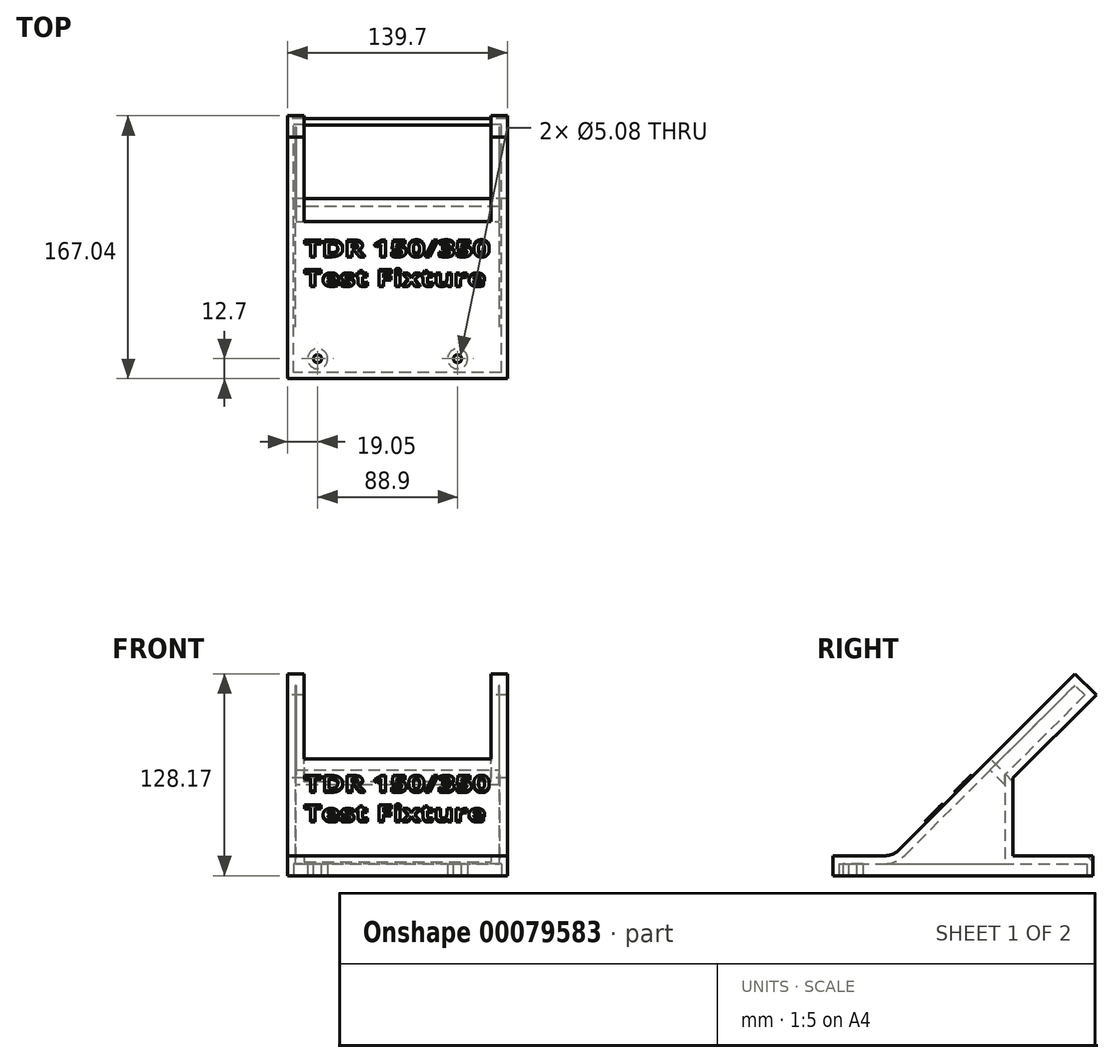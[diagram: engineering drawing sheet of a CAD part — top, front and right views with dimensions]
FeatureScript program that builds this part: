
annotation { "Feature Type Name" : "Feature", "Feature Type Description" : "" }
export const myFeature = defineFeature(function(context is Context, id is Id, definition is map)
    precondition{}
    {
        {
            var Q0;
            Q0=qCreatedBy(makeId("Right.planeOp"),FACE);
            var sketch = newSketch(context, id + "F0", { "sketchPlane" : qUnion([Q0])});
            skLineSegment(sketch, "E0.bottom", {"start": v(0, 0) * mm, "end": v(165.1, 0) * mm});
            skLineSegment(sketch, "E0.top", {"start": v(0, 12.7) * mm, "end": v(32.84, 12.7) * mm});
            skLineSegment(sketch, "E0.left", {"start": v(0, 0) * mm, "end": v(0, 12.7) * mm});
            skLineSegment(sketch, "E0.right", {"start": v(165.1, 0) * mm, "end": v(165.1, 12.7) * mm});
            skLineSegment(sketch, "E1", {"start": v(41.82, 16.42) * mm, "end": v(145.86, 120.46) * mm});
            skLineSegment(sketch, "E2.0", {"start": v(114.33, 61.98) * mm, "end": v(167.04, 114.7) * mm});
            skLineSegment(sketch, "E3.trimOffspring", {"start": v(114.33, 12.7) * mm, "end": v(165.1, 12.7) * mm});
            skPoint(sketch, "E4.visualSharp", {"position": v(38.1, 12.7) * mm});
            skArc(sketch, "E4.filletArc", {"start": v(32.84, 12.7) * mm, "mid": v(37.7, 13.67) * mm, "end": v(41.82, 16.42) * mm});
            skPoint(sketch, "E5.visualSharp", {"position": v(65.04, 12.7) * mm});
            skLineSegment(sketch, "E6", {"start": v(145.86, 120.46) * mm, "end": v(153.57, 128.17) * mm});
            skLineSegment(sketch, "E7", {"start": v(167.04, 114.7) * mm, "end": v(153.57, 128.17) * mm});
            skLineSegment(sketch, "E8", {"start": v(114.33, 61.98) * mm, "end": v(114.33, 12.7) * mm});
            skSolve(sketch);
        }
        {
            var Q0;
            Q0=makeQuery(id+"F0.imprint","IMPRINT",FACE,{"disambiguationData":[TD([[makeQuery(id+"F0.imprint","IMPRINT",EDGE,{"derivedFrom":sQuery(id+"F0.wireOp",EDGE,"E0.bottom")}),1.0]])]});
            extrude(context, id + "F1", {"entities" : qUnion([Q0]), "depth" : 139.7 * mm, "offsetDistance" : 25.4 * mm});
        }
        {
            var Q0;
            Q0=makeQuery(id+"F1.opExtrude","SWEPT_FACE",FACE,{"disambiguationData":[OSD([sQuery(id+"F0.wireOp",EDGE,"E1")])]});
            var sketch = newSketch(context, id + "F2", { "sketchPlane" : qUnion([Q0])});
            skLineSegment(sketch, "E9.bottom", {"start": v(129.29, 199.22) * mm, "end": v(10.41, 199.22) * mm});
            skLineSegment(sketch, "E9.top", {"start": v(10.41, 123.02) * mm, "end": v(129.29, 123.02) * mm});
            skLineSegment(sketch, "E9.left", {"start": v(129.29, 199.22) * mm, "end": v(129.29, 123.02) * mm});
            skLineSegment(sketch, "E9.right", {"start": v(10.41, 199.22) * mm, "end": v(10.41, 123.02) * mm});
            skSolve(sketch);
        }
        {
            var Q0;
            Q0=makeQuery(id+"F2.imprint","IMPRINT",FACE,{"disambiguationData":[TD([[makeQuery(id+"F2.imprint","IMPRINT",EDGE,{"derivedFrom":sQuery(id+"F2.wireOp",EDGE,"E9.bottom")}),1.0]])]});
            extrude(context, id + "F3", {"entities" : qUnion([Q0]), "operationType" : NewBodyOperationType.REMOVE, "endBound" : BoundingType.THROUGH_ALL, "oppositeDirection" : true, "depth" : 25.4 * mm});
        }
        {
            var Q0;
            Q0=makeQuery(id+"F1.opExtrude","SWEPT_FACE",FACE,{"disambiguationData":[OSD([sQuery(id+"F0.wireOp",EDGE,"E0.top")])]});
            var sketch = newSketch(context, id + "F4", { "sketchPlane" : qUnion([Q0])});
            skCircle(sketch, "E10", {"center": v(19.05, 12.7) * mm, "radius": 2.54 * mm});
            skCircle(sketch, "E11", {"center": v(107.95, 12.7) * mm, "radius": 2.54 * mm});
            skSolve(sketch);
        }
        {
            var Q0;
            Q0=makeQuery(id+"F4.imprint","IMPRINT",FACE,{"disambiguationData":[TD([[makeQuery(id+"F4.imprint","IMPRINT",EDGE,{"derivedFrom":sQuery(id+"F4.wireOp",EDGE,"E10")}),1.0]])]});
            var Q1;
            Q1=makeQuery(id+"F4.imprint","IMPRINT",FACE,{"disambiguationData":[TD([[makeQuery(id+"F4.imprint","IMPRINT",EDGE,{"derivedFrom":sQuery(id+"F4.wireOp",EDGE,"E11")}),1.0]])]});
            extrude(context, id + "F5", {"entities" : qUnion([Q0, Q1]), "operationType" : NewBodyOperationType.REMOVE, "endBound" : BoundingType.THROUGH_ALL, "oppositeDirection" : true, "depth" : 25.4 * mm});
        }
        {
            var Q0;
            {var subQ0=sQuery(id+"F0.wireOp",EDGE,"E7");Q0=makeQuery(id+"F3.boolean.opBoolean","SPLIT",FACE,{"disambiguationData":[TD([makeQuery(id+"F3.opExtrude","SWEPT_FACE",FACE,{"disambiguationData":[OSD([sQuery(id+"F2.wireOp",EDGE,"E9.left")])]})])],"derivedFrom":makeQuery(id+"F1.opExtrude","SWEPT_FACE",FACE,{"disambiguationData":[OSD([subQ0])]})});}
            var sketch = newSketch(context, id + "F6", { "sketchPlane" : qUnion([Q0])});
            skLineSegment(sketch, "E12.bottom", {"start": v(132.84, 23.8) * mm, "end": v(6.86, 23.8) * mm});
            skLineSegment(sketch, "E12.top", {"start": v(132.84, 30.15) * mm, "end": v(6.86, 30.15) * mm});
            skLineSegment(sketch, "E12.left", {"start": v(132.84, 23.8) * mm, "end": v(132.84, 30.15) * mm});
            skLineSegment(sketch, "E12.right", {"start": v(6.86, 23.8) * mm, "end": v(6.86, 30.15) * mm});
            skSolve(sketch);
        }
        {
            var Q0;
            {var subQ0=sQuery(id+"F6.wireOp",EDGE,"E12.right");Q0=makeQuery(id+"F6.imprint","IMPRINT",FACE,{"disambiguationData":[TD([[makeQuery(id+"F6.imprint","IMPRINT",EDGE,{"derivedFrom":subQ0}),-1.0]])]});}
            var Q1;
            {var subQ0=sQuery(id+"F6.wireOp",EDGE,"E12.left");Q1=makeQuery(id+"F6.imprint","IMPRINT",FACE,{"disambiguationData":[TD([[makeQuery(id+"F6.imprint","IMPRINT",EDGE,{"derivedFrom":subQ0}),1.0]])]});}
            extrude(context, id + "F7", {"entities" : qUnion([Q0, Q1]), "operationType" : NewBodyOperationType.REMOVE, "oppositeDirection" : true, "depth" : 76.2 * mm, "offsetDistance" : 25.4 * mm});
        }
        {
            var Q0;
            Q0=makeQuery(id+"F1.opExtrude","SWEPT_FACE",FACE,{"disambiguationData":[OSD([sQuery(id+"F0.wireOp",EDGE,"E0.bottom")])]});
            var sketch = newSketch(context, id + "F8", { "sketchPlane" : qUnion([Q0])});
            skLineSegment(sketch, "E13.0", {"start": v(3.81, -3.81) * mm, "end": v(3.81, -161.29) * mm});
            skLineSegment(sketch, "E13.1", {"start": v(135.9, -3.81) * mm, "end": v(3.8, -3.81) * mm});
            skLineSegment(sketch, "E13.2", {"start": v(135.9, -3.81) * mm, "end": v(135.9, -161.29) * mm});
            skLineSegment(sketch, "E13.3", {"start": v(135.9, -161.29) * mm, "end": v(3.8, -161.29) * mm});
            skCircle(sketch, "E14.0", {"center": v(107.95, -12.7) * mm, "radius": 6.35 * mm});
            skCircle(sketch, "E15.0", {"center": v(19.05, -12.7) * mm, "radius": 6.35 * mm});
            skSolve(sketch);
        }
        {
            var Q0;
            Q0=makeQuery(id+"F8.imprint","IMPRINT",FACE,{"disambiguationData":[TD([[makeQuery(id+"F8.imprint","IMPRINT",EDGE,{"derivedFrom":sQuery(id+"F8.wireOp",EDGE,"E13.0")}),1.0]])]});
            extrude(context, id + "F9", {"entities" : qUnion([Q0]), "operationType" : NewBodyOperationType.REMOVE, "oppositeDirection" : true, "depth" : 7.62 * mm});
        }
        {
            var Q0;
            Q0=makeQuery(id+"F9.boolean.opBoolean","COPY",FACE,{"derivedFrom":makeQuery(id+"F9.opExtrude","CAP_FACE",FACE,{"disambiguationData":[OSD([sQuery(id+"F8.wireOp",EDGE,"E13.0"),sQuery(id+"F8.wireOp",EDGE,"E13.1"),sQuery(id+"F8.wireOp",EDGE,"E13.2"),sQuery(id+"F8.wireOp",EDGE,"E13.3"),sQuery(id+"F8.wireOp",EDGE,"E14.0"),sQuery(id+"F8.wireOp",EDGE,"E15.0"),sQuery(id+"F8.wireOp",EDGE,"036abaf6-195f-4b96-b425-33d400b71304.0"),sQuery(id+"F8.wireOp",EDGE,"614a8467-6721-4685-bece-80110cc94b02.0")])],"isStart":false})});
            shell(context, id + "F10", {"entities" : qUnion([Q0]), "thickness" : 5.08 * mm});
        }
        {
            var Q0;
            Q0=makeQuery(id+"F1.opExtrude","SWEPT_FACE",FACE,{"disambiguationData":[OSD([sQuery(id+"F0.wireOp",EDGE,"E1"),sQuery(id+"F0.wireOp",EDGE,"E6")])]});
            var sketch = newSketch(context, id + "F11", { "sketchPlane" : qUnion([Q0])});
            skText(sketch, "E16", { "text": "TDR 150/350 \nTest Fixture", "fontName": "OpenSans-Bold.ttf"});
            const initialGuessF11  = {"E16": [0.01041, 0.09282, 1, 0, 0.01402]};
            skSetInitialGuess(sketch, initialGuessF11);
            skSolve(sketch);
        }
        {
            var Q0;
            Q0 = qSketchRegion(id + "F11", true);
            extrude(context, id + "F12", {"entities" : qUnion([Q0]), "operationType" : NewBodyOperationType.ADD, "depth" : 1.27 * mm, "offsetDistance" : 25.4 * mm});
        }
    });
